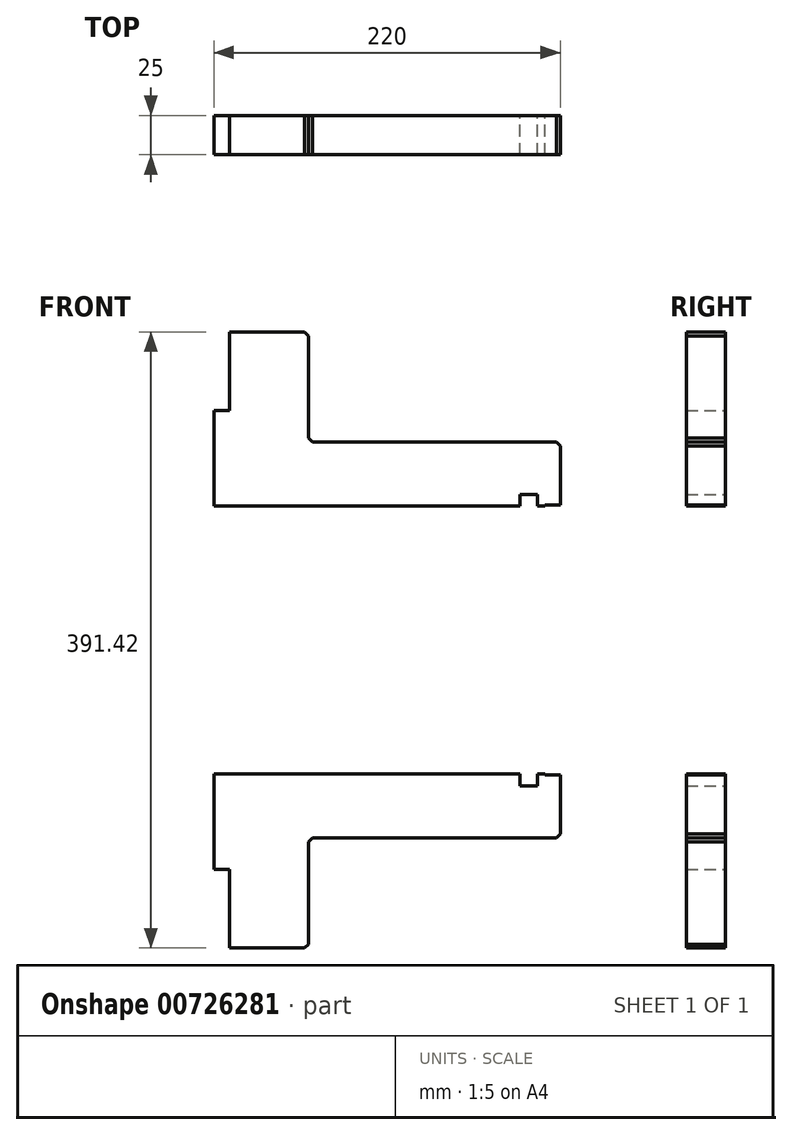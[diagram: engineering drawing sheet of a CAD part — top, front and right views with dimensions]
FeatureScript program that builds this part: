
annotation { "Feature Type Name" : "Feature", "Feature Type Description" : "" }
export const myFeature = defineFeature(function(context is Context, id is Id, definition is map)
    precondition{}
    {
        {
            var Q0;
            Q0=qCreatedBy(makeId("Front.planeOp"),FACE);
            var sketch = newSketch(context, id + "F0", { "sketchPlane" : qUnion([Q0])});
            skLineSegment(sketch, "E0", {"start": v(0, 0) * mm, "end": v(0, 55) * mm});
            skLineSegment(sketch, "E1", {"start": v(0, 55) * mm, "end": v(10, 55) * mm});
            skLineSegment(sketch, "E2", {"start": v(10, 55) * mm, "end": v(10, 105) * mm});
            skLineSegment(sketch, "E3", {"start": v(10, 105) * mm, "end": v(60, 105) * mm});
            skLineSegment(sketch, "E4", {"start": v(60, 105) * mm, "end": v(60, 35) * mm});
            skLineSegment(sketch, "E5", {"start": v(60, 35) * mm, "end": v(220, 35) * mm});
            skLineSegment(sketch, "E6", {"start": v(220, 35) * mm, "end": v(220, -5) * mm});
            skLineSegment(sketch, "E7", {"start": v(220, -5) * mm, "end": v(210.4, -5) * mm});
            skLineSegment(sketch, "E8", {"start": v(210.4, -5) * mm, "end": v(210.4, -5.65) * mm});
            skLineSegment(sketch, "E9", {"start": v(210.4, -5.64) * mm, "end": v(205.4, -5.64) * mm});
            skLineSegment(sketch, "E10", {"start": v(205.4, -5.64) * mm, "end": v(205.4, 1.86) * mm});
            skLineSegment(sketch, "E11", {"start": v(205.4, 1.86) * mm, "end": v(194.3, 1.86) * mm});
            skLineSegment(sketch, "E12", {"start": v(194.3, 1.86) * mm, "end": v(194.3, -5.64) * mm});
            skLineSegment(sketch, "E13", {"start": v(194.3, -5.64) * mm, "end": v(0, -5.64) * mm});
            skLineSegment(sketch, "E14", {"start": v(0, -5.64) * mm, "end": v(0, 0) * mm});
            skLineSegment(sketch, "E15", {"start": v(0, -90.7) * mm, "end": v(243.6, -90.7) * mm, "construction": true});
            skLineSegment(sketch, "E16.MirrorCS", {"start": v(210.4, -176.42) * mm, "end": v(210.4, -175.77) * mm});
            skLineSegment(sketch, "E17.MirrorCS", {"start": v(210.4, -175.77) * mm, "end": v(205.4, -175.77) * mm});
            skLineSegment(sketch, "E18.MirrorCS", {"start": v(194.3, -183.27) * mm, "end": v(194.3, -175.77) * mm});
            skLineSegment(sketch, "E19.MirrorCS", {"start": v(205.4, -175.77) * mm, "end": v(205.4, -183.27) * mm});
            skLineSegment(sketch, "E20.MirrorCS", {"start": v(0, -175.77) * mm, "end": v(0, -181.42) * mm});
            skLineSegment(sketch, "E21.MirrorCS", {"start": v(220, -176.42) * mm, "end": v(210.4, -176.42) * mm});
            skLineSegment(sketch, "E22.MirrorCS", {"start": v(205.4, -183.27) * mm, "end": v(194.3, -183.27) * mm});
            skLineSegment(sketch, "E23.MirrorCS", {"start": v(0, -181.42) * mm, "end": v(0, -236.42) * mm});
            skLineSegment(sketch, "E24.MirrorCS", {"start": v(0, -236.42) * mm, "end": v(10, -236.42) * mm});
            skLineSegment(sketch, "E25.MirrorCS", {"start": v(10, -236.42) * mm, "end": v(10, -286.42) * mm});
            skLineSegment(sketch, "E26.MirrorCS", {"start": v(220, -216.42) * mm, "end": v(220, -176.42) * mm});
            skLineSegment(sketch, "E27.MirrorCS", {"start": v(60, -216.42) * mm, "end": v(220, -216.42) * mm});
            skLineSegment(sketch, "E28.MirrorCS", {"start": v(194.3, -175.77) * mm, "end": v(0, -175.77) * mm});
            skLineSegment(sketch, "E29.MirrorCS", {"start": v(60, -286.42) * mm, "end": v(60, -216.42) * mm});
            skLineSegment(sketch, "E30.MirrorCS", {"start": v(10, -286.42) * mm, "end": v(60, -286.42) * mm});
            skSolve(sketch);
        }
        {
            var Q0;
            Q0=makeQuery(id+"F0.imprint","IMPRINT",FACE,{"disambiguationData":[TD([[makeQuery(id+"F0.imprint","IMPRINT",EDGE,{"derivedFrom":sQuery(id+"F0.wireOp",EDGE,"E0")}),-1.0]])]});
            var Q1;
            Q1=makeQuery(id+"F0.imprint","IMPRINT",FACE,{"disambiguationData":[TD([[makeQuery(id+"F0.imprint","IMPRINT",EDGE,{"derivedFrom":sQuery(id+"F0.wireOp",EDGE,"E16.MirrorCS")}),1.0]])]});
            extrude(context, id + "F1", {"entities" : qUnion([Q0, Q1]), "depth" : 25 * mm, "offsetDistance" : 25 * mm});
        }
        {
            var Q0;
            Q0=makeQuery(id+"F1.opExtrude","SWEPT_EDGE",EDGE,{"disambiguationData":[OSD([sQuery(id+"F0.wireOp",EDGE,"E4"),sQuery(id+"F0.wireOp",EDGE,"E5")])]});
            var Q1;
            Q1=makeQuery(id+"F1.opExtrude","SWEPT_EDGE",EDGE,{"disambiguationData":[OSD([sQuery(id+"F0.wireOp",EDGE,"E5"),sQuery(id+"F0.wireOp",EDGE,"E6")])]});
            var Q2;
            Q2=makeQuery(id+"F1.opExtrude","SWEPT_EDGE",EDGE,{"disambiguationData":[OSD([sQuery(id+"F0.wireOp",EDGE,"E3"),sQuery(id+"F0.wireOp",EDGE,"E4")])]});
            var Q3;
            Q3=makeQuery(id+"F1.opExtrude","SWEPT_EDGE",EDGE,{"disambiguationData":[OSD([sQuery(id+"F0.wireOp",EDGE,"E26.MirrorCS"),sQuery(id+"F0.wireOp",EDGE,"E27.MirrorCS")])]});
            var Q4;
            Q4=makeQuery(id+"F1.opExtrude","SWEPT_EDGE",EDGE,{"disambiguationData":[OSD([sQuery(id+"F0.wireOp",EDGE,"E27.MirrorCS"),sQuery(id+"F0.wireOp",EDGE,"E29.MirrorCS")])]});
            var Q5;
            Q5=makeQuery(id+"F1.opExtrude","SWEPT_EDGE",EDGE,{"disambiguationData":[OSD([sQuery(id+"F0.wireOp",EDGE,"E29.MirrorCS"),sQuery(id+"F0.wireOp",EDGE,"E30.MirrorCS")])]});
            chamfer(context, id + "F2", {"entities" : qUnion([Q0, Q1, Q2, Q3, Q4, Q5]), "width" : 2.5 * mm, "tangentPropagation" : true});
        }
    });
